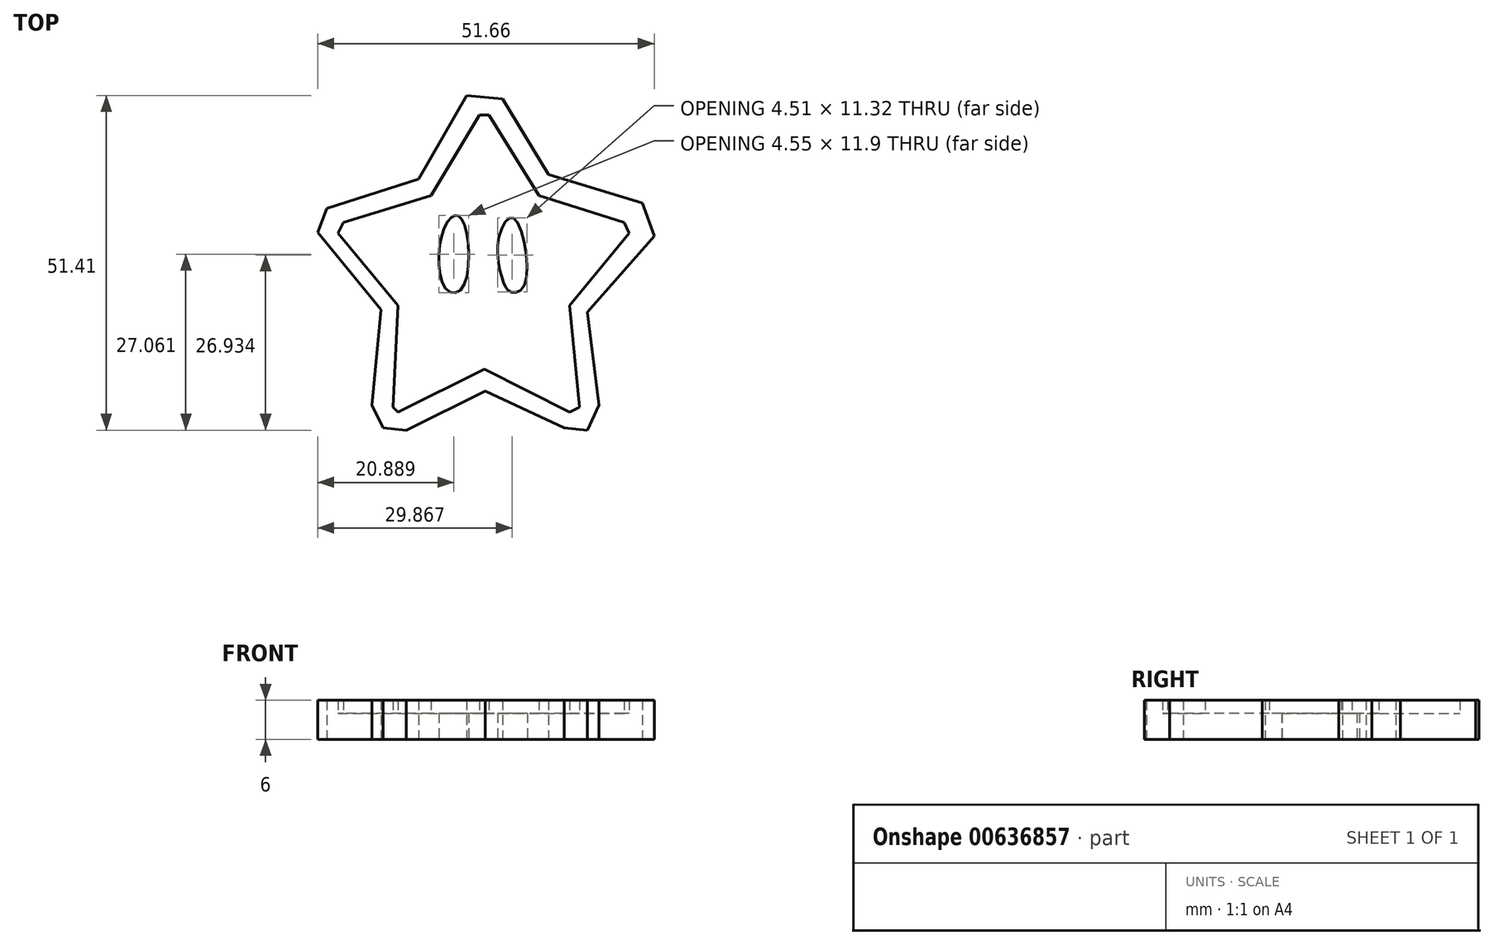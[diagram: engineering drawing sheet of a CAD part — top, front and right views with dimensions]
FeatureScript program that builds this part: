
annotation { "Feature Type Name" : "Feature", "Feature Type Description" : "" }
export const myFeature = defineFeature(function(context is Context, id is Id, definition is map)
    precondition{}
    {
        {
            var Q0;
            Q0=qCreatedBy(makeId("Top.planeOp"),FACE);
            var sketch = newSketch(context, id + "F0", { "sketchPlane" : qUnion([Q0])});
            skLineSegment(sketch, "E0", {"start": v(19.84, 43.23) * mm, "end": v(5.73, 38.7) * mm});
            skLineSegment(sketch, "E1", {"start": v(5.73, 38.7) * mm, "end": v(4.32, 35.04) * mm});
            skLineSegment(sketch, "E2", {"start": v(4.32, 35.04) * mm, "end": v(14.05, 23.18) * mm});
            skLineSegment(sketch, "E3", {"start": v(14.05, 23.18) * mm, "end": v(12.64, 8.5) * mm});
            skLineSegment(sketch, "E4", {"start": v(12.64, 8.5) * mm, "end": v(14.34, 4.97) * mm});
            skLineSegment(sketch, "E5", {"start": v(14.34, 4.97) * mm, "end": v(17.9, 4.63) * mm});
            skLineSegment(sketch, "E6", {"start": v(17.9, 4.63) * mm, "end": v(30, 10.62) * mm});
            skLineSegment(sketch, "E7", {"start": v(30, 10.62) * mm, "end": v(42.14, 4.97) * mm});
            skLineSegment(sketch, "E8", {"start": v(42.14, 4.97) * mm, "end": v(45.7, 4.63) * mm});
            skLineSegment(sketch, "E9", {"start": v(45.7, 4.63) * mm, "end": v(47.5, 8.5) * mm});
            skLineSegment(sketch, "E10", {"start": v(47.5, 8.5) * mm, "end": v(45.7, 22.76) * mm});
            skLineSegment(sketch, "E11", {"start": v(45.7, 22.76) * mm, "end": v(55.98, 34.48) * mm});
            skLineSegment(sketch, "E12", {"start": v(55.98, 34.48) * mm, "end": v(54.14, 39.56) * mm});
            skLineSegment(sketch, "E13", {"start": v(54.14, 39.56) * mm, "end": v(39.74, 43.93) * mm});
            skLineSegment(sketch, "E14", {"start": v(39.74, 43.93) * mm, "end": v(32.69, 55.5) * mm});
            skLineSegment(sketch, "E15", {"start": v(32.69, 55.5) * mm, "end": v(27.17, 56.04) * mm});
            skLineSegment(sketch, "E16", {"start": v(27.17, 56.04) * mm, "end": v(19.84, 43.23) * mm});
            skFitSpline(sketch, "E17", {"points": [v(25.38, 37.64) * mm, v(23.28, 34.28) * mm, v(24.04, 26.31) * mm, v(26.47, 26.4) * mm, v(26.9, 36.05) * mm, v(25.38, 37.64) * mm]});
            skFitSpline(sketch, "E18", {"points": [v(34.36, 37.22) * mm, v(32.1, 34.03) * mm, v(32.77, 27.57) * mm, v(33.94, 25.9) * mm, v(36.12, 27.07) * mm, v(34.36, 37.22) * mm]});
            skLineSegment(sketch, "E19", {"start": v(8.26, 36.55) * mm, "end": v(7.42, 34.87) * mm});
            skLineSegment(sketch, "E20", {"start": v(7.42, 34.87) * mm, "end": v(16.65, 23.8) * mm});
            skLineSegment(sketch, "E21", {"start": v(16.65, 23.8) * mm, "end": v(15.9, 8.18) * mm});
            skLineSegment(sketch, "E22", {"start": v(15.9, 8.18) * mm, "end": v(16.65, 7.43) * mm});
            skLineSegment(sketch, "E23", {"start": v(16.65, 7.43) * mm, "end": v(29.94, 14) * mm});
            skLineSegment(sketch, "E24", {"start": v(29.94, 14) * mm, "end": v(43, 7.43) * mm});
            skLineSegment(sketch, "E25", {"start": v(43, 7.43) * mm, "end": v(44.53, 8.18) * mm});
            skLineSegment(sketch, "E26", {"start": v(44.53, 8.18) * mm, "end": v(43, 23.8) * mm});
            skLineSegment(sketch, "E27", {"start": v(43, 23.8) * mm, "end": v(52.15, 34.87) * mm});
            skLineSegment(sketch, "E28", {"start": v(52.15, 34.87) * mm, "end": v(51.34, 36.52) * mm});
            skLineSegment(sketch, "E29", {"start": v(51.34, 36.52) * mm, "end": v(38.3, 40.66) * mm});
            skLineSegment(sketch, "E30", {"start": v(38.3, 40.66) * mm, "end": v(31.56, 51.5) * mm});
            skLineSegment(sketch, "E31", {"start": v(31.56, 51.5) * mm, "end": v(30.57, 53.08) * mm});
            skLineSegment(sketch, "E32", {"start": v(30.57, 53.08) * mm, "end": v(29.12, 53.08) * mm});
            skLineSegment(sketch, "E33", {"start": v(29.12, 53.08) * mm, "end": v(21.7, 40.66) * mm});
            skLineSegment(sketch, "E34", {"start": v(21.7, 40.66) * mm, "end": v(8.26, 36.55) * mm});
            skSolve(sketch);
        }
        {
            var Q0;
            Q0=makeQuery(id+"F0.imprint","IMPRINT",FACE,{"disambiguationData":[TD([[makeQuery(id+"F0.imprint","IMPRINT",EDGE,{"derivedFrom":sQuery(id+"F0.wireOp",EDGE,"E17")}),-1.0]])]});
            extrude(context, id + "F1", {"entities" : qUnion([Q0]), "depth" : 4 * mm, "offsetDistance" : 25 * mm});
        }
        {
            var Q0;
            Q0 = qSketchRegion(id + "F0", true);
            extrude(context, id + "F2", {"entities" : qUnion([Q0]), "operationType" : NewBodyOperationType.ADD, "depth" : 6 * mm, "offsetDistance" : 25 * mm});
        }
        {
            var Q0;
            Q0=sQuery(id+"F0.wireOp",EDGE,"E17");
            var Q1;
            Q1=sQuery(id+"F0.wireOp",EDGE,"E18");
            extrude(context, id + "F3", {"bodyType" : ToolBodyType.SURFACE, "surfaceEntities" : qUnion([Q0, Q1]), "depth" : 6 * mm, "offsetDistance" : 25 * mm});
        }
    });
